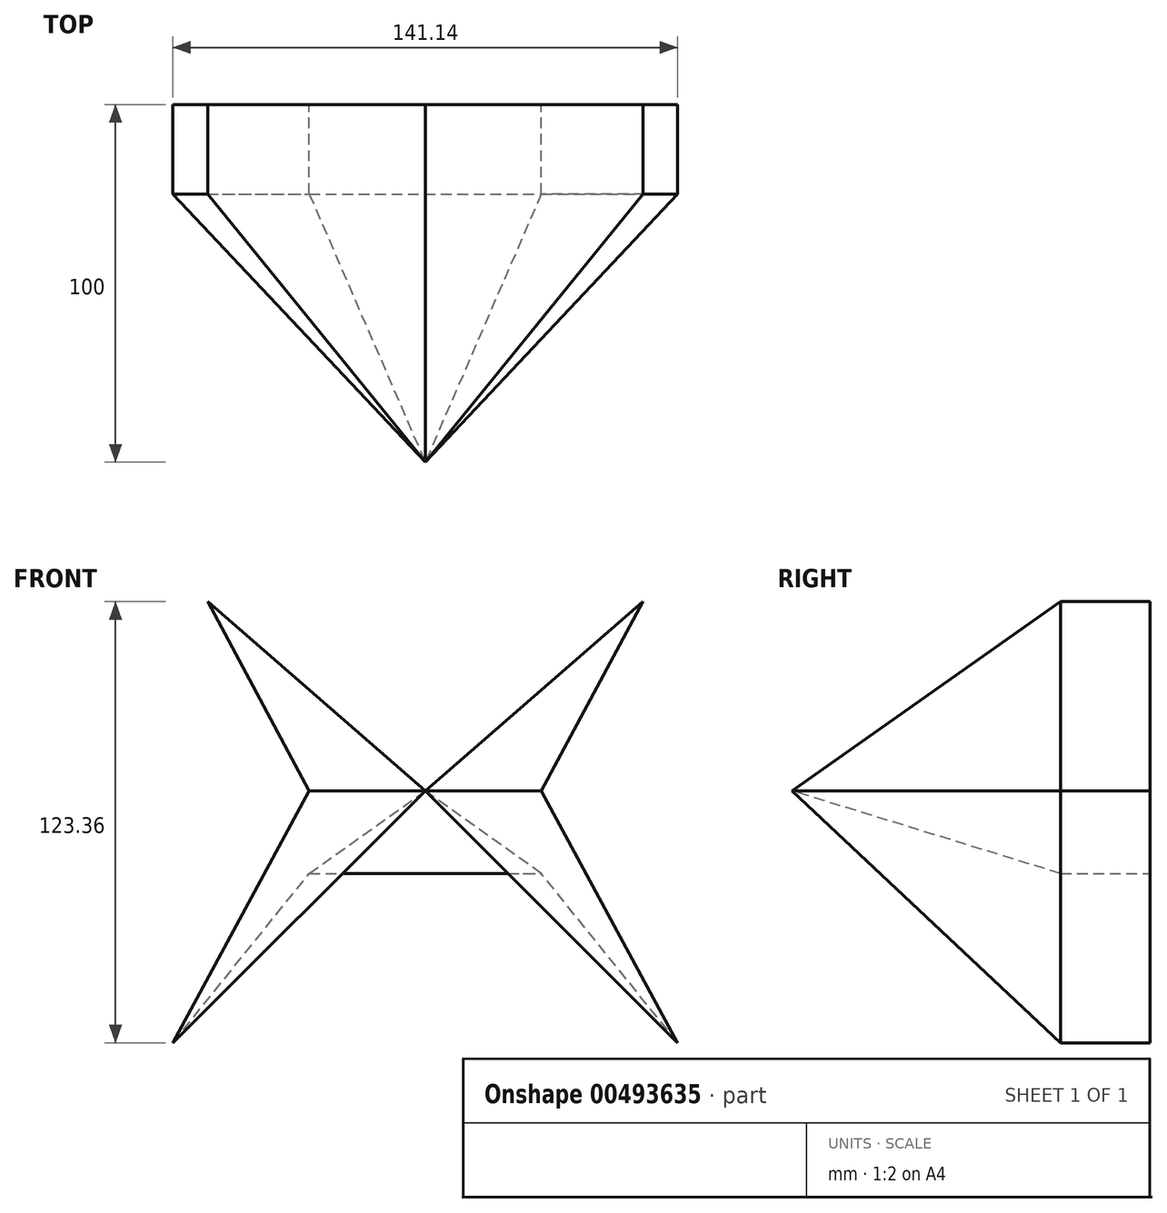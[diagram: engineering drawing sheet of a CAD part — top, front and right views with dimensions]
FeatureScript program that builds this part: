
annotation { "Feature Type Name" : "Feature", "Feature Type Description" : "" }
export const myFeature = defineFeature(function(context is Context, id is Id, definition is map)
    precondition{}
    {
        {
            var Q0;
            Q0=qCreatedBy(makeId("Front.planeOp"),FACE);
            var sketch = newSketch(context, id + "F0", { "sketchPlane" : qUnion([Q0])});
            skLineSegment(sketch, "E0", {"start": v(0, 0) * mm, "end": v(60.82, 52.93) * mm});
            skLineSegment(sketch, "E1", {"start": v(60.82, 52.93) * mm, "end": v(32.42, 0) * mm});
            skLineSegment(sketch, "E2", {"start": v(32.42, 0) * mm, "end": v(70.57, -70.43) * mm});
            skLineSegment(sketch, "E3", {"start": v(70.57, -70.43) * mm, "end": v(32.42, -23.1) * mm});
            skLineSegment(sketch, "E4.MirrorCS", {"start": v(0, 0) * mm, "end": v(-60.82, 52.93) * mm});
            skLineSegment(sketch, "E5.MirrorCS", {"start": v(-60.82, 52.93) * mm, "end": v(-32.42, 0) * mm});
            skLineSegment(sketch, "E6.MirrorCS", {"start": v(-32.42, 0) * mm, "end": v(-70.57, -70.43) * mm});
            skLineSegment(sketch, "E7.MirrorCS", {"start": v(-70.57, -70.43) * mm, "end": v(-32.42, -23.1) * mm});
            skLineSegment(sketch, "E8", {"start": v(-32.42, -23.1) * mm, "end": v(32.42, -23.1) * mm});
            skSolve(sketch);
        }
        {
            var Q0;
            Q0=makeQuery(id+"F0.imprint","IMPRINT",FACE,{"disambiguationData":[TD([[makeQuery(id+"F0.imprint","IMPRINT",EDGE,{"derivedFrom":sQuery(id+"F0.wireOp",EDGE,"E0")}),-1.0]])]});
            extrude(context, id + "F1", {"entities" : qUnion([Q0]), "depth" : 25 * mm});
        }
        {
            var Q0;
            Q0=qCreatedBy(makeId("Front.planeOp"),FACE);
            cPlane(context, id + "F2", {"entities" : qUnion([Q0]), "cplaneType" : CPlaneType.OFFSET, "offset" : 100 * mm, "width" : 150 * mm, "height" : 150 * mm});
        }
        {
            var Q0;
            Q0=qCreatedBy(id+"F2.planeOp",FACE);
            var sketch = newSketch(context, id + "F3", { "sketchPlane" : qUnion([Q0])});
            skPoint(sketch, "E9", {"position": v(0, 0) * mm});
            skSolve(sketch);
        }
        {
            var Q1;
            Q1=makeQuery(id+"F1.opExtrude","CAP_FACE",FACE,{"disambiguationData":[OSD([sQuery(id+"F0.wireOp",EDGE,"E0"),sQuery(id+"F0.wireOp",EDGE,"E1"),sQuery(id+"F0.wireOp",EDGE,"E2"),sQuery(id+"F0.wireOp",EDGE,"E3"),sQuery(id+"F0.wireOp",EDGE,"E4.MirrorCS"),sQuery(id+"F0.wireOp",EDGE,"E5.MirrorCS"),sQuery(id+"F0.wireOp",EDGE,"E7.MirrorCS"),sQuery(id+"F0.wireOp",EDGE,"E6.MirrorCS"),sQuery(id+"F0.wireOp",EDGE,"E8")])],"isStart":false});
            var Q2;
            Q2=sQuery(id+"F3.wireOp",VERTEX,"E9");
            loft(context, id + "F4", {"operationType" : NewBodyOperationType.ADD, "sheetProfilesArray" : [{ "sheetProfileEntities" : qUnion([Q1]) }, { "sheetProfileEntities" : qUnion([Q2]) }]});
        }
    });
